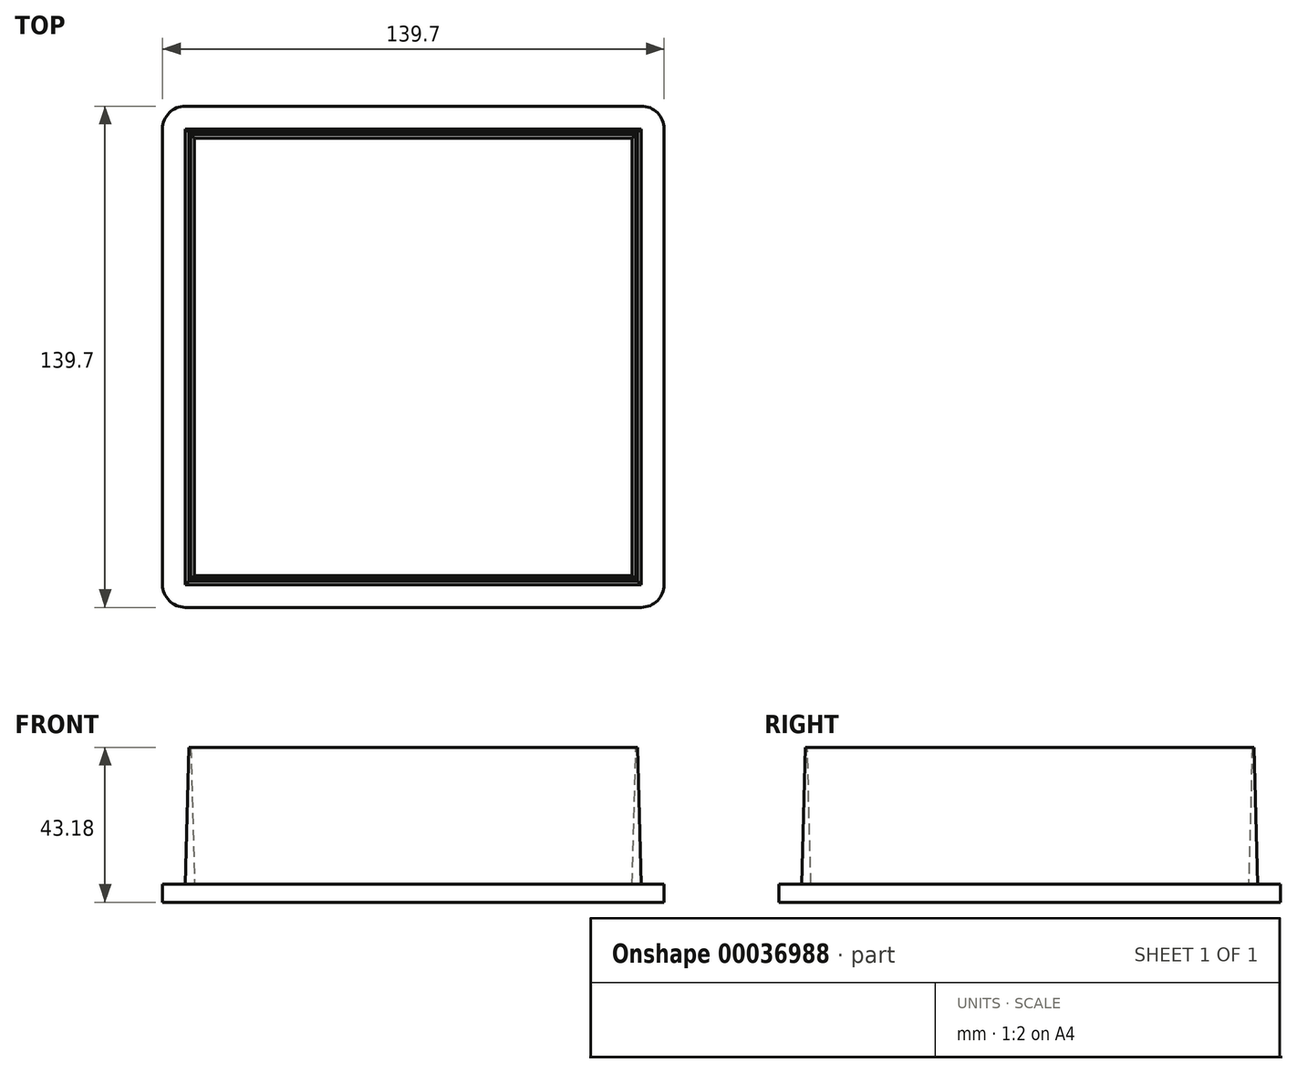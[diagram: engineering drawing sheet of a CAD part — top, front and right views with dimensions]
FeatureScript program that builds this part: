
annotation { "Feature Type Name" : "Feature", "Feature Type Description" : "" }
export const myFeature = defineFeature(function(context is Context, id is Id, definition is map)
    precondition{}
    {
        {
            var Q0;
            Q0=qCreatedBy(makeId("Top.planeOp"),FACE);
            var sketch = newSketch(context, id + "F0", { "sketchPlane" : qUnion([Q0])});
            skLineSegment(sketch, "E0.rect.bottom", {"start": v(63.5, 63.5) * mm, "end": v(-63.5, 63.5) * mm});
            skLineSegment(sketch, "E0.rect.top", {"start": v(63.5, -63.5) * mm, "end": v(-63.5, -63.5) * mm});
            skLineSegment(sketch, "E0.rect.left", {"start": v(63.5, 63.5) * mm, "end": v(63.5, -63.5) * mm});
            skLineSegment(sketch, "E0.rect.right", {"start": v(-63.5, 63.5) * mm, "end": v(-63.5, -63.5) * mm});
            skPoint(sketch, "E0.rect.middle", {"position": v(0, 0) * mm});
            skLineSegment(sketch, "E1.0", {"start": v(-60.96, 60.96) * mm, "end": v(-60.96, -60.96) * mm});
            skLineSegment(sketch, "E1.1", {"start": v(60.96, 60.96) * mm, "end": v(-60.96, 60.96) * mm});
            skLineSegment(sketch, "E1.2", {"start": v(60.96, 60.96) * mm, "end": v(60.96, -60.96) * mm});
            skLineSegment(sketch, "E1.3", {"start": v(60.96, -60.96) * mm, "end": v(-60.96, -60.96) * mm});
            skSolve(sketch);
        }
        {
            var Q0;
            Q0=makeQuery(id+"F0.imprint","IMPRINT",FACE,{"disambiguationData":[TD([[makeQuery(id+"F0.imprint","IMPRINT",EDGE,{"derivedFrom":sQuery(id+"F0.wireOp",EDGE,"E0.rect.bottom")}),1.0]])]});
            extrude(context, id + "F1", {"entities" : qUnion([Q0]), "depth" : 38.1 * mm, "hasDraft" : true, "draftAngle" : 1.5 * degree, "draftPullDirection" : true});
        }
        {
            var Q0;
            Q0=qCreatedBy(makeId("Top.planeOp"),FACE);
            var sketch = newSketch(context, id + "F2", { "sketchPlane" : qUnion([Q0])});
            skLineSegment(sketch, "E2.rect.bottom", {"start": v(69.85, -69.85) * mm, "end": v(-69.85, -69.85) * mm});
            skLineSegment(sketch, "E2.rect.top", {"start": v(69.85, 69.85) * mm, "end": v(-69.85, 69.85) * mm});
            skLineSegment(sketch, "E2.rect.left", {"start": v(69.85, -69.85) * mm, "end": v(69.85, 69.85) * mm});
            skLineSegment(sketch, "E2.rect.right", {"start": v(-69.85, -69.85) * mm, "end": v(-69.85, 69.85) * mm});
            skPoint(sketch, "E2.rect.middle", {"position": v(0, 0) * mm});
            skSolve(sketch);
        }
        {
            var Q0;
            Q0 = qSketchRegion(id + "F2", true);
            extrude(context, id + "F3", {"entities" : qUnion([Q0]), "operationType" : NewBodyOperationType.ADD, "oppositeDirection" : true, "depth" : 5.08 * mm});
        }
        {
            var Q0;
            Q0=makeQuery(id+"F3.opExtrude","SWEPT_EDGE",EDGE,{"disambiguationData":[OSD([sQuery(id+"F2.wireOp",EDGE,"E2.rect.top"),sQuery(id+"F2.wireOp",EDGE,"E2.rect.right")])]});
            var Q1;
            Q1=makeQuery(id+"F3.opExtrude","SWEPT_EDGE",EDGE,{"disambiguationData":[OSD([sQuery(id+"F2.wireOp",EDGE,"E2.rect.bottom"),sQuery(id+"F2.wireOp",EDGE,"E2.rect.right")])]});
            var Q2;
            Q2=makeQuery(id+"F3.opExtrude","SWEPT_EDGE",EDGE,{"disambiguationData":[OSD([sQuery(id+"F2.wireOp",EDGE,"E2.rect.bottom"),sQuery(id+"F2.wireOp",EDGE,"E2.rect.left")])]});
            var Q3;
            Q3=makeQuery(id+"F3.opExtrude","SWEPT_EDGE",EDGE,{"disambiguationData":[OSD([sQuery(id+"F2.wireOp",EDGE,"E2.rect.top"),sQuery(id+"F2.wireOp",EDGE,"E2.rect.left")])]});
            fillet(context, id + "F4", {"entities" : qUnion([Q0, Q1, Q2, Q3]), "radius" : 6.35 * mm, "tangentPropagation" : true, "allowEdgeOverflow" : false});
        }
    });
